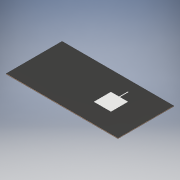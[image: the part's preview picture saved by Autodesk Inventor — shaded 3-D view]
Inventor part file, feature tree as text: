
AUTODESK INVENTOR PART (.ipt)
format: ipt  version: 2017 (Build 210142000, 142)  size: 122,368 bytes
history: native  units: in
note: dims shown in document units (in); Inventor stores cm internally (conversion verified against a paired STEP export)
features: extrude x2, sketch x2
ambient origin geometry x8: Origin, YZ Plane, XZ Plane, XY Plane, X Axis, Y Axis, Z Axis, Center Point
bodies: Solid1 (feature_tree)
feature tree (4):
  extrude  "Extrusion1"  Depth=48.0in
  extrude  "Extrusion2"  Depth=0.001in
  sketch  "Sketch1"  dims[d0=96.0in d1=48.0in]
  sketch  "Sketch2"  dims[d2=0.5in d3=0.0in d4=1.5in d5=1.5in d6=21.0in d7=7.5in d8=15.0in d9=15.0in d10=7.5in d11=90.0deg d12=0.5in d13=7.5in d14=0.001in d15=0.0in]
